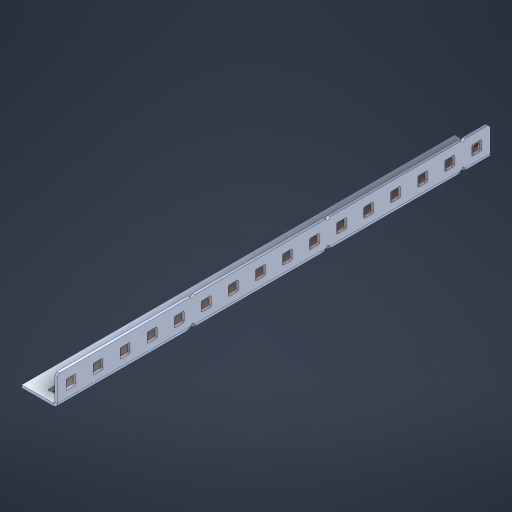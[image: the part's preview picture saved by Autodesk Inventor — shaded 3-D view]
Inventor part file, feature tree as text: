
AUTODESK INVENTOR PART (.ipt)
format: ipt  version: 2023 (Build 270158000, 158)  size: 685,056 bytes
history: native  units: in
note: dims shown in document units (in); Inventor stores cm internally (conversion verified against a paired STEP export)
features: other x37, extrude x31, sheet_metal_op x10, sketch x8, mirror x1, pattern_linear x1, chamfer x1
ambient origin geometry x8: Origin, YZ Plane, XZ Plane, XY Plane, X Axis, Y Axis, Z Axis, Center Point
bodies: Solid1 (feature_tree), Body (feature_tree)
feature tree (89):
  other  "Flange Pattern Plane"
  sheet_metal_op  "Flange Pattern"
  sheet_metal_op  "Body Pattern"
  other  "Arc Length"
  mirror  "Notch Mirror"
  pattern_linear  "Notch Pattern"  Spacing1=0.1875in  [1 undecoded]
  chamfer  "End Chamfer"
  extrude  "Half Cut"  Depth=0.0469in
  sketch  "Sketch1"  dims[d0=2.5in]
  other  "Plate1"
  sketch  "Sketch2"  dims[d1=8.0in]
  other  "Plate2"
  sheet_metal_op  "Bend1"
  sheet_metal_op  "Corner1"
  sketch  "Sketch3"  dims[d2=0.0469in]
  other  "Flange Pattern Sketch"
  sketch  "Sketch7"  dims[d3=0.0469in]
  other  "Srf1"
  other  "Srf2"
  sketch  "Sketch8"  dims[d4=0.0234in]
  sketch  "Sketch9"  dims[d5=0.0938in]
  other  "Srf91"
  sheet_metal_op  "Body Pattern Sketch"
  other  "Srf92"
  sketch  "Sketch13"  dims[d6=0.0469in]
  sketch  "Sketch14"  dims[d7=0.5in d8=90.0deg d9=0.0312in d10=0.1875in d11=0.0469in d12=0.0469in d16=0.182in d17=0.02in d18=0.0469in d19=0.0in d20=0.25in d21=0.25in d46=0.172in d47=1.0in d48=0.0in d49=0.182in d50=0.02in d51=0.25in d52=0.25in d53=0.0469in d54=0.0in d55=0.172in d56=1.0in d57=0.0in d60=6.2992in d62=0.5in d63=0.3937in d65=0.5in d85=0.1227in d86=0.1659in d88=0.04in d89=0.0469in d90=0.0in d91=0.04in d92=0.0491in d95=2.5in d96=0.04in d97=0.25in d98=45.0deg d101=0.0in d102=2.497in d131=0.5in d132=6.2992in d134=0.5in d139=0.5in]
  other  "Srf856"
  other  "Srf1310"
  other  "Srf1311"
  other  "Srf1312"
  other  "Srf1376"
  other  "Srf1377"
  other  "Srf1728"
  other  "Srf1755"
  other  "Srf1878"
  other  "Srf1879"
  other  "Srf1880"
  other  "Srf1881"
  other  "Srf1882"
  other  "Srf1883"
  other  "Srf1884"
  other  "Srf1885"
  other  "Srf1886"
  other  "Srf1887"
  other  "Srf1942"
  other  "Srf1943"
  other  "Srf1944"
  other  "Srf1945"
  other  "Srf1946"
  other  "Srf1947"
  other  "Srf1948"
  other  "Srf1949"
  other  "Srf1950"
  other  "Srf1951"
  sheet_metal_op  "Flange Stamp"
  sheet_metal_op  "Flange Circle"
  sheet_metal_op  "Body Stamp"
  sheet_metal_op  "Body Circle"
  sheet_metal_op  "Notch"
  extrude  "ExtrusionSrf2"  Depth=0.0469in
  extrude  "ExtrusionSrf92"  Depth=0.5in
  extrude  "ExtrusionSrf856"  Depth=0.02in
  extrude  "ExtrusionSrf1310"  Depth=0.0469in
  extrude  "ExtrusionSrf1311"  TaperAngle=0.0deg  [1 undecoded]
  extrude  "ExtrusionSrf1312"  Depth=0.5in
  extrude  "ExtrusionSrf1376"  Depth=0.5in
  extrude  "ExtrusionSrf1377"  Depth=0.5in
  extrude  "ExtrusionSrf1728"  Depth=0.5in TaperAngle=0.0deg
  extrude  "ExtrusionSrf1755"  Depth=0.5in
  extrude  "ExtrusionSrf1878"  Depth=0.02in
  extrude  "ExtrusionSrf1879"  Depth=0.5in
  extrude  "ExtrusionSrf1880"  Depth=0.5in
  extrude  "ExtrusionSrf1881"  Depth=0.0469in
  extrude  "ExtrusionSrf1882"  TaperAngle=0.0deg  [1 undecoded]
  extrude  "ExtrusionSrf1883"  Depth=0.5in
  extrude  "ExtrusionSrf1884"  Depth=0.5in TaperAngle=0.0deg
  extrude  "ExtrusionSrf1885"  Depth=0.5in
  extrude  "ExtrusionSrf1886"  Depth=0.5in
  extrude  "ExtrusionSrf1887"  Depth=0.5in
  extrude  "ExtrusionSrf1942"  Depth=0.5in
  extrude  "ExtrusionSrf1943"  Depth=0.5in
  extrude  "ExtrusionSrf1944"  Depth=0.0469in
  extrude  "ExtrusionSrf1945"  TaperAngle=0.0deg  [1 undecoded]
  extrude  "ExtrusionSrf1946"  Depth=0.5in
  extrude  "ExtrusionSrf1947"  Depth=0.5in
  extrude  "ExtrusionSrf1948"  Depth=0.5in
  extrude  "ExtrusionSrf1949"  Depth=0.5in TaperAngle=45.0deg
  extrude  "ExtrusionSrf1950"  TaperAngle=0.0deg  [1 undecoded]
  extrude  "ExtrusionSrf1951"  Depth=0.5in
note: 5 required parameter values undecoded (feature->parameter linkage not recoverable at this tier; creation-order binding heuristic only, values carry confidence <= 0.55)
